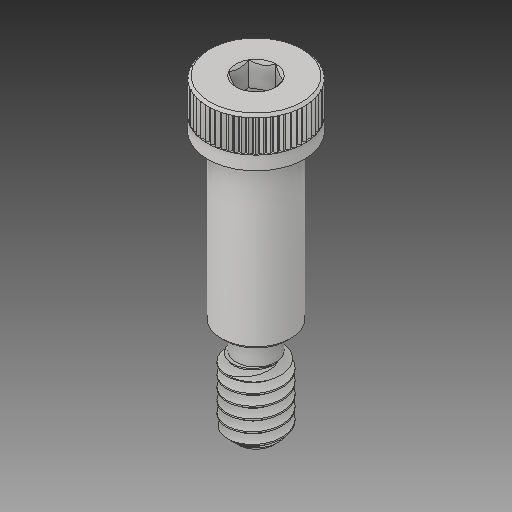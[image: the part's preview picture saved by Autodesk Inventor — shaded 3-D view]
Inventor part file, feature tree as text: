
AUTODESK INVENTOR PART (.ipt)
format: ipt  version: 2017 (Build 210142000, 142)  size: 580,608 bytes
history: mixed  units: in
note: dims shown in document units (in); Inventor stores cm internally (conversion verified against a paired STEP export)
features: chamfer x1, imported_body x1
ambient origin geometry x8: Origin, YZ Plane, XZ Plane, XY Plane, X Axis, Y Axis, Z Axis, Center Point
bodies: Solid1 (imported_parasolid)
feature tree (2):
  chamfer  "Chamfer3"  [1 undecoded]
  imported_body  NMx_Import_Brep_tag  [imported B-rep: ~22 faces, bbox_mm=[8.672971, 24.60625, 9.101667]]
note: 1 required parameter value undecoded (feature->parameter linkage not recoverable at this tier; creation-order binding heuristic only, values carry confidence <= 0.55)
